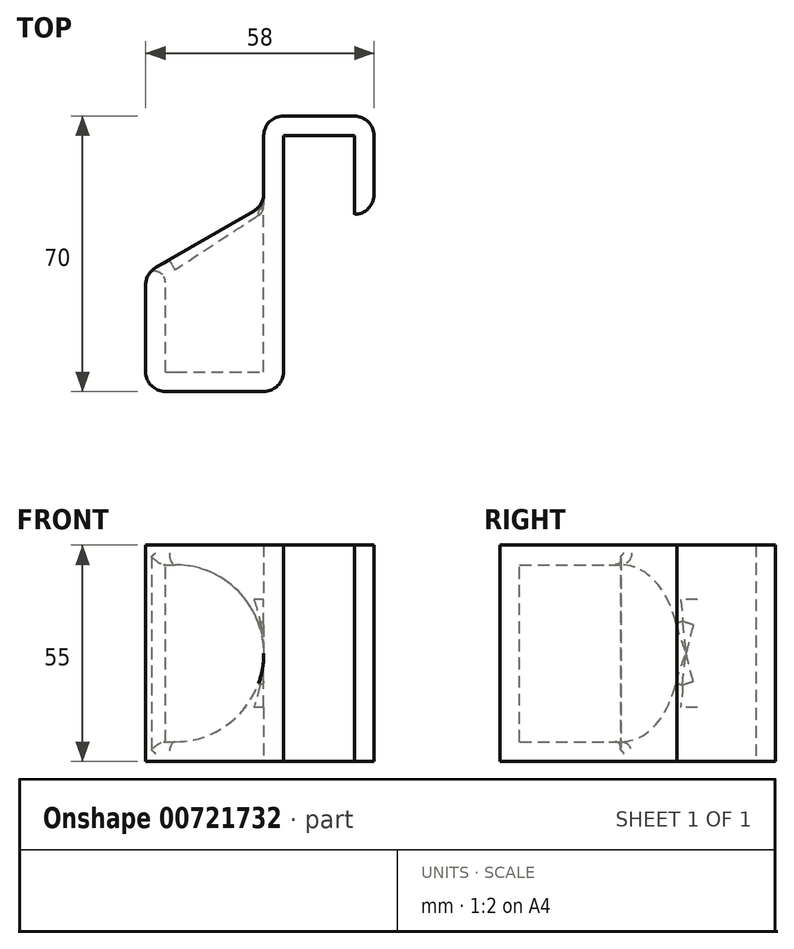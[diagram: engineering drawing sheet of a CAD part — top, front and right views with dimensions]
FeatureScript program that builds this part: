
annotation { "Feature Type Name" : "Feature", "Feature Type Description" : "" }
export const myFeature = defineFeature(function(context is Context, id is Id, definition is map)
    precondition{}
    {
        {
            var Q0;
            Q0=qCreatedBy(makeId("Top.planeOp"),FACE);
            var sketch = newSketch(context, id + "F0", { "sketchPlane" : qUnion([Q0])});
            skLineSegment(sketch, "E0", {"start": v(0, 0) * mm, "end": v(18, 0) * mm});
            skLineSegment(sketch, "E1", {"start": v(18, 0) * mm, "end": v(18, -20) * mm});
            skLineSegment(sketch, "E2", {"start": v(0, 0) * mm, "end": v(0, -65) * mm});
            skLineSegment(sketch, "E3.0", {"start": v(23, 5) * mm, "end": v(23, -20) * mm});
            skLineSegment(sketch, "E3.1", {"start": v(-5, 5) * mm, "end": v(23, 5) * mm});
            skLineSegment(sketch, "E3.2", {"start": v(-5, 5) * mm, "end": v(-5, -17.68) * mm});
            skLineSegment(sketch, "E4", {"start": v(18, -20) * mm, "end": v(23, -20) * mm});
            skLineSegment(sketch, "E5", {"start": v(0, -65) * mm, "end": v(-35, -65) * mm});
            skLineSegment(sketch, "E6", {"start": v(-35, -65) * mm, "end": v(-35, -35) * mm});
            skLineSegment(sketch, "E7", {"start": v(-35, -35) * mm, "end": v(-5, -17.68) * mm});
            skSolve(sketch);
        }
        {
            var Q0;
            Q0=makeQuery(id+"F0.imprint","IMPRINT",FACE,{"disambiguationData":[TD([[makeQuery(id+"F0.imprint","IMPRINT",EDGE,{"derivedFrom":sQuery(id+"F0.wireOp",EDGE,"E0")}),1.0]])]});
            extrude(context, id + "F1", {"entities" : qUnion([Q0]), "depth" : 55 * mm, "offsetDistance" : 25 * mm});
        }
        {
            var Q0;
            Q0=qCreatedBy(makeId("Front.planeOp"),FACE);
            var Q1;
            Q1=makeQuery(id+"F1.opExtrude","CAP_VERTEX",VERTEX,{"disambiguationData":[OSD([sQuery(id+"F0.wireOp",EDGE,"E3.2"),sQuery(id+"F0.wireOp",EDGE,"E7")])],"isStart":false});
            cPlane(context, id + "F2", {"entities" : qUnion([Q0, Q1]), "cplaneType" : CPlaneType.PLANE_POINT, "offset" : 25 * mm, "width" : 150 * mm, "height" : 150 * mm});
        }
        {
            var Q0;
            Q0=qCreatedBy(id+"F2.planeOp",FACE);
            var sketch = newSketch(context, id + "F3", { "sketchPlane" : qUnion([Q0])});
            skLineSegment(sketch, "E8", {"start": v(-30, 5) * mm, "end": v(-30, 50) * mm});
            skArc(sketch, "E9", {"start": v(-27.5, 5) * mm, "mid": v(-5, 27.5) * mm, "end": v(-27.5, 50) * mm});
            skLineSegment(sketch, "E10", {"start": v(-30, 50) * mm, "end": v(-27.5, 50) * mm});
            skLineSegment(sketch, "E11", {"start": v(-30, 5) * mm, "end": v(-27.5, 5) * mm});
            skSolve(sketch);
        }
        {
            var Q0;
            Q0=makeQuery(id+"F1.opExtrude","SWEPT_FACE",FACE,{"disambiguationData":[OSD([sQuery(id+"F0.wireOp",EDGE,"E5")])]});
            cPlane(context, id + "F4", {"entities" : qUnion([Q0]), "cplaneType" : CPlaneType.OFFSET, "offset" : 5 * mm, "oppositeDirection" : true, "width" : 150 * mm, "height" : 150 * mm});
        }
        {
            var Q0;
            Q0=makeQuery(id+"F3.imprint","IMPRINT",FACE,{"disambiguationData":[TD([[makeQuery(id+"F3.imprint","IMPRINT",EDGE,{"derivedFrom":sQuery(id+"F3.wireOp",EDGE,"E8")}),-1.0]])]});
            var Q1;
            Q1=qCreatedBy(id+"F4.planeOp",FACE);
            extrude(context, id + "F5", {"entities" : qUnion([Q0]), "operationType" : NewBodyOperationType.REMOVE, "endBound" : BoundingType.UP_TO_SURFACE, "depth" : 35 * mm, "endBoundEntityFace" : qUnion([Q1]), "offsetDistance" : 25 * mm});
        }
        {
            var Q0;
            Q0=makeQuery(id+"F5.boolean.opBoolean","INTERSECT",EDGE,{"disambiguationData":[OD(0.0)],"derivedFrom":[makeQuery(id+"F1.opExtrude","SWEPT_FACE",FACE,{"disambiguationData":[OSD([sQuery(id+"F0.wireOp",EDGE,"E7")])]}),makeQuery(id+"F5.opExtrude","SWEPT_FACE",FACE,{"disambiguationData":[OSD([sQuery(id+"F3.wireOp",EDGE,"E9")])]})]});
            var Q1;
            Q1=makeQuery(id+"F5.boolean.opBoolean","INTERSECT",EDGE,{"derivedFrom":[makeQuery(id+"F1.opExtrude","SWEPT_FACE",FACE,{"disambiguationData":[OSD([sQuery(id+"F0.wireOp",EDGE,"E7")])]}),makeQuery(id+"F5.opExtrude","SWEPT_FACE",FACE,{"disambiguationData":[OSD([sQuery(id+"F3.wireOp",EDGE,"E8")])]})]});
            fillet(context, id + "F6", {"entities" : qUnion([Q0, Q1]), "radius" : 3 * mm, "tangentPropagation" : true, "allowEdgeOverflow" : false});
        }
        {
            var Q0;
            Q0=makeQuery(id+"F1.opExtrude","SWEPT_EDGE",EDGE,{"disambiguationData":[OSD([sQuery(id+"F0.wireOp",EDGE,"E3.2"),sQuery(id+"F0.wireOp",EDGE,"E7")])]});
            var Q1;
            Q1=makeQuery(id+"F1.opExtrude","SWEPT_EDGE",EDGE,{"disambiguationData":[OSD([sQuery(id+"F0.wireOp",EDGE,"E3.1"),sQuery(id+"F0.wireOp",EDGE,"E3.2")])]});
            var Q2;
            Q2=makeQuery(id+"F1.opExtrude","SWEPT_EDGE",EDGE,{"disambiguationData":[OSD([sQuery(id+"F0.wireOp",EDGE,"E3.0"),sQuery(id+"F0.wireOp",EDGE,"E3.1")])]});
            var Q3;
            Q3=makeQuery(id+"F1.opExtrude","SWEPT_EDGE",EDGE,{"disambiguationData":[OSD([sQuery(id+"F0.wireOp",EDGE,"E3.0"),sQuery(id+"F0.wireOp",EDGE,"E4")])]});
            var Q4;
            Q4=makeQuery(id+"F1.opExtrude","SWEPT_EDGE",EDGE,{"disambiguationData":[OSD([sQuery(id+"F0.wireOp",EDGE,"E5"),sQuery(id+"F0.wireOp",EDGE,"E6")])]});
            var Q5;
            Q5=makeQuery(id+"F1.opExtrude","SWEPT_EDGE",EDGE,{"disambiguationData":[OSD([sQuery(id+"F0.wireOp",EDGE,"E2"),sQuery(id+"F0.wireOp",EDGE,"E5")])]});
            var Q6;
            Q6=makeQuery(id+"F1.opExtrude","SWEPT_EDGE",EDGE,{"disambiguationData":[OSD([sQuery(id+"F0.wireOp",EDGE,"E6"),sQuery(id+"F0.wireOp",EDGE,"E7")])]});
            fillet(context, id + "F7", {"entities" : qUnion([Q0, Q1, Q2, Q3, Q4, Q5, Q6]), "radius" : 5 * mm, "tangentPropagation" : true, "allowEdgeOverflow" : false});
        }
    });
